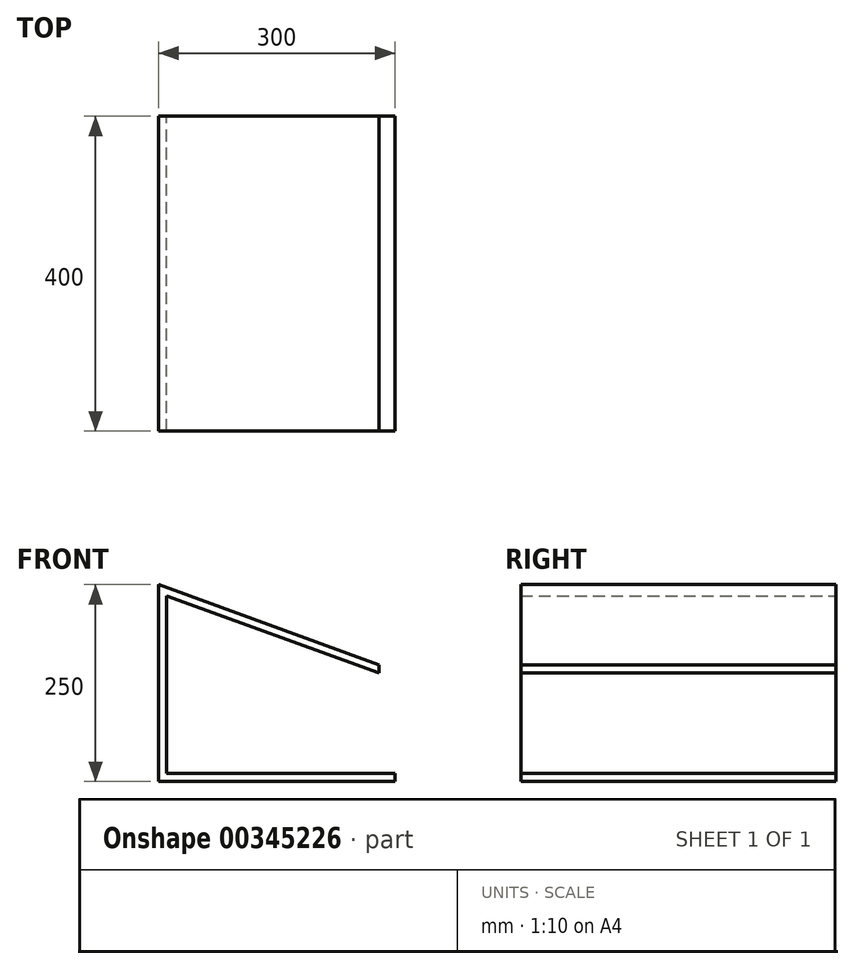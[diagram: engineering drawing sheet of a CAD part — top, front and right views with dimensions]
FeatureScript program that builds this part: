
annotation { "Feature Type Name" : "Feature", "Feature Type Description" : "" }
export const myFeature = defineFeature(function(context is Context, id is Id, definition is map)
    precondition{}
    {
        {
            var Q0;
            Q0=qCreatedBy(makeId("Front.planeOp"),FACE);
            var sketch = newSketch(context, id + "F0", { "sketchPlane" : qUnion([Q0])});
            skLineSegment(sketch, "E0.top", {"start": v(-150, -125) * mm, "end": v(150, -125) * mm});
            skLineSegment(sketch, "E0.left", {"start": v(-150, 125) * mm, "end": v(-150, -125) * mm});
            skLineSegment(sketch, "E0.right", {"start": v(150, -115) * mm, "end": v(150, -125) * mm});
            skPoint(sketch, "E0.middle", {"position": v(0, 0) * mm});
            skLineSegment(sketch, "E1", {"start": v(-150, 125) * mm, "end": v(130, 23.09) * mm});
            skLineSegment(sketch, "E2", {"start": v(-140, -115) * mm, "end": v(-140, 110.72) * mm});
            skLineSegment(sketch, "E3.trimOffspring", {"start": v(-140, 110.72) * mm, "end": v(130, 12.45) * mm});
            skLineSegment(sketch, "E4", {"start": v(130, 23.09) * mm, "end": v(130, 12.45) * mm});
            skLineSegment(sketch, "E5", {"start": v(-140, -115) * mm, "end": v(150, -115) * mm});
            skSolve(sketch);
        }
        {
            var Q0;
            Q0=qSketchRegion(id+"F0",true);
            extrude(context, id + "F1", {"entities" : qUnion([Q0]), "depth" : 400 * mm});
        }
    });
